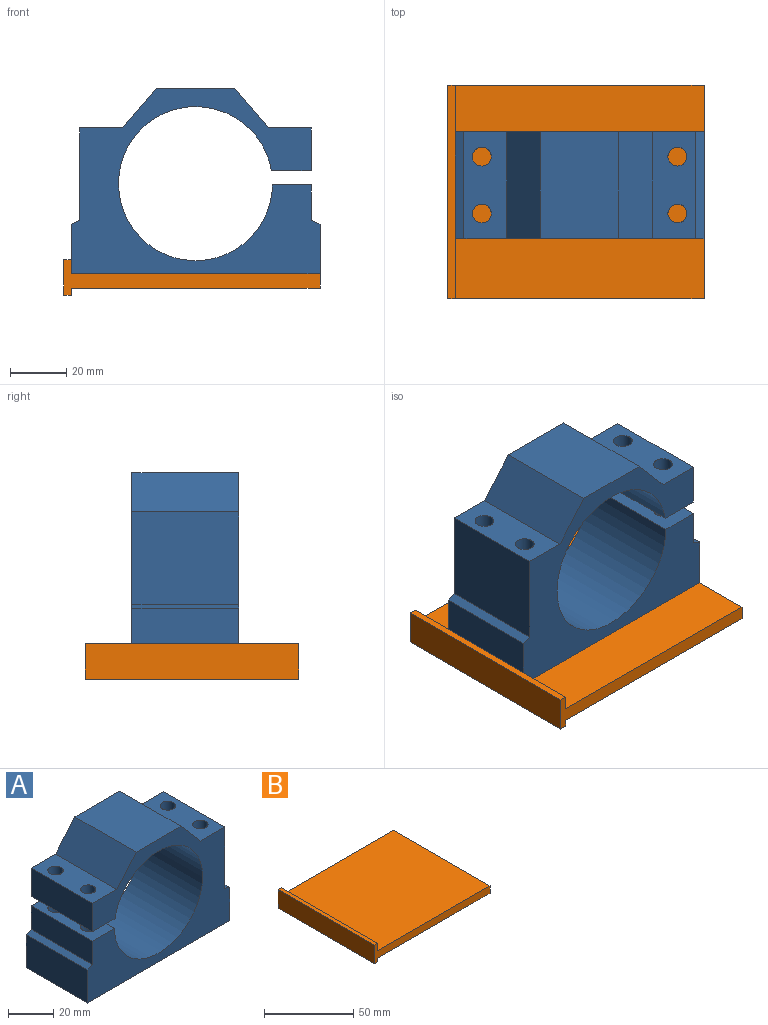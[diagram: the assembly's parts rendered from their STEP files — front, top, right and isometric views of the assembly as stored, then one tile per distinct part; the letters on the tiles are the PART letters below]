
ASSEMBLY  parts=2 mates=2
PART A: 24 faces, bbox 88.9x38.1x66 mm
  f0: plane 38.1x15.24mm, normal (-1,0,0), area 580.6mm2, adj f1,f2,f10,f17
  f1: plane 88.9x66.04mm, normal (0,-1,0), area 2527.8mm2, adj f0,f3,f4,f5,f6,f7,f8,f9
  f2: plane 88.9x66.04mm, normal (0,1,0), area 2527.8mm2, adj f0,f3,f4,f5,f6,f7,f8,f9
  f3: plane 38.1x17.78mm, normal (1,0,0), area 677.4mm2, adj f1,f2,f4,f15
  f4: plane 38.1x3.18mm, normal (0.37,0,0.93), area 130.3mm2, adj f1,f2,f3,f5
  f5: plane 38.1x33.02mm, normal (1,0,0), area 1258.1mm2, adj f1,f2,f4,f6
  f6: plane 38.1x15.24mm, normal (0,0,1), area 508.9mm2, adj f1,f2,f5,f7,f22,f23
  f7: plane 38.1x13.97mm, normal (0.76,0,0.65), area 703.3mm2, adj f1,f2,f6,f8
  f8: plane 38.1x27.94mm, normal (0,0,1), area 1064.5mm2, adj f1,f2,f7,f9
  f9: plane 38.1x13.97mm, normal (-0.76,0,0.65), area 703.3mm2, adj f1,f2,f8,f10
  f10: plane 38.1x15.24mm, normal (0,0,1), area 508.9mm2, adj f0,f1,f2,f9,f18,f20
  f11: plane 38.1x12.7mm, normal (-1,0,0), area 483.9mm2, adj f1,f2,f12,f16
  f12: plane 38.1x3.18mm, normal (-0.37,0,0.93), area 130.3mm2, adj f1,f2,f11,f13
  f13: plane 38.1x17.78mm, normal (-1,0,0), area 677.4mm2, adj f1,f2,f12,f15
  f14: cylinder r=27.5mm len=55mm, axis (0,1,0), area 6388.8mm2, adj f1,f2,f16,f17
  f15: plane 88.9x38.1mm, normal (0,0,-1), area 3243.7mm2, adj f1,f2,f3,f13,f19,f21,f22,f23
  f16: plane 38.1x13.78mm, normal (0,0,1), area 453.3mm2, adj f1,f2,f11,f14,f19,f21
  f17: plane 38.1x14.17mm, normal (0,0,-1), area 468.1mm2, adj f0,f1,f2,f14,f18,f20
  f18: cylinder r=3.38mm len=15.24mm, axis (0,0,1), area 323.5mm2, adj f10,f17
  f19: cylinder r=3.38mm len=31.75mm, axis (0,0,1), area 673.9mm2, adj f15,f16
  f20: cylinder r=3.38mm len=15.24mm, axis (0,0,1), area 323.5mm2, adj f10,f17
  f21: cylinder r=3.38mm len=31.75mm, axis (0,0,1), area 673.9mm2, adj f15,f16
  f22: cylinder r=3.38mm len=52.07mm, axis (0,0,1), area 1105.2mm2, adj f6,f15
  f23: cylinder r=3.38mm len=52.07mm, axis (0,0,1), area 1105.2mm2, adj f6,f15
PART B: 10 faces, bbox 91.4x76.2x12.7 mm
  f0: plane 76.2x12.7mm, normal (-1,0,0), area 967.7mm2, adj f1,f7,f8,f9
  f1: plane 76.2x2.54mm, normal (0,0,-1), area 193.5mm2, adj f0,f2,f8,f9
  f2: plane 76.2x2.54mm, normal (1,0,0), area 193.5mm2, adj f1,f3,f8,f9
  f3: plane 88.9x76.2mm, normal (0,0,-1), area 6774.2mm2, adj f2,f4,f8,f9
  f4: plane 76.2x5.08mm, normal (1,0,0), area 387.1mm2, adj f3,f5,f8,f9
  f5: plane 88.9x76.2mm, normal (0,0,1), area 6774.2mm2, adj f4,f6,f8,f9
  f6: plane 76.2x5.08mm, normal (1,0,0), area 387.1mm2, adj f5,f7,f8,f9
  f7: plane 76.2x2.54mm, normal (0,0,1), area 193.5mm2, adj f0,f6,f8,f9
  f8: plane 91.44x12.7mm, normal (0,-1,0), area 483.9mm2, adj f0,f1,f2,f3,f4,f5,f6,f7
  f9: plane 91.44x12.7mm, normal (0,1,0), area 483.9mm2, adj f0,f1,f2,f3,f4,f5,f6,f7
PLACE A rot(axis=(0,0,-1),180deg) t=(46.99,21.45,7.62)mm
PLACE B t=(0,76.2,2.54)mm
MATE planar A.f23 <-> B.f5  axis (0,0,-1) through (12.06,50.66,7.62)mm
MATE planar B.f6 <-> A.f3  axis (1,0,0) through (2.54,38.1,10.16)mm
